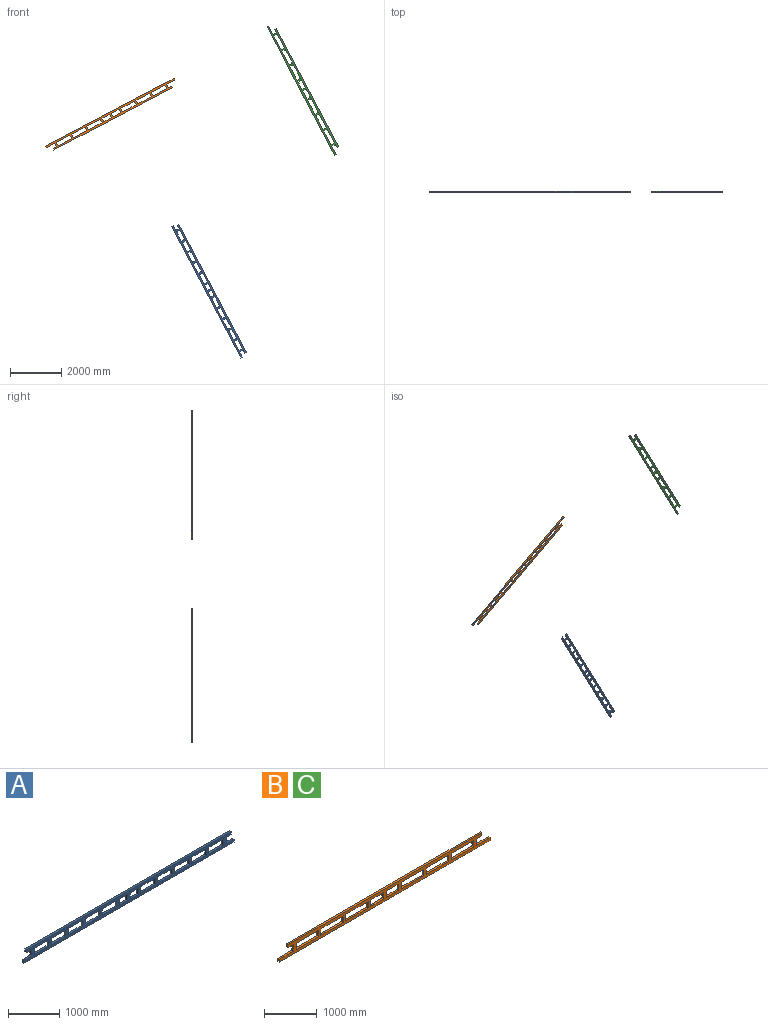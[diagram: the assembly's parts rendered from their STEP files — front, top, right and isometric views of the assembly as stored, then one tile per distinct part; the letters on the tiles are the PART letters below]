
ASSEMBLY  parts=3 mates=2
PART A: 62 faces, bbox 5800x45x290 mm
  f0: plane 400x45mm, normal (0,0,-1), area 18000mm2, adj f17,f18,f19,f23
  f1: plane 400x45mm, normal (0,0,-1), area 18000mm2, adj f17,f18,f22,f26
  f2: plane 400x45mm, normal (0,0,-1), area 18000mm2, adj f17,f18,f25,f29
  f3: plane 400x45mm, normal (0,0,-1), area 18000mm2, adj f17,f18,f28,f32
  f4: plane 400x45mm, normal (0,0,-1), area 18000mm2, adj f17,f18,f31,f35
  f5: plane 150x45mm, normal (0,0,-1), area 6750mm2, adj f14,f17,f18,f34
  f6: plane 225x45mm, normal (0,0,-1), area 10125mm2, adj f17,f18,f37,f59
  f7: plane 400x45mm, normal (0,0,-1), area 18000mm2, adj f17,f18,f38,f40
  f8: plane 400x45mm, normal (0,0,-1), area 18000mm2, adj f17,f18,f41,f52
  f9: plane 400x45mm, normal (0,0,-1), area 18000mm2, adj f17,f18,f53,f54
  f10: plane 400x45mm, normal (0,0,-1), area 18000mm2, adj f17,f18,f55,f56
  f11: plane 225x45mm, normal (0,0,-1), area 10125mm2, adj f17,f18,f20,f58
  f12: plane 400x45mm, normal (0,0,-1), area 18000mm2, adj f17,f18,f57,f60
  f13: plane 5660x45mm, normal (0,0,1), area 254700mm2, adj f14,f16,f17,f18
  f14: plane 70x45mm, normal (-1,0,0), area 3150mm2, adj f5,f13,f17,f18
  f15: plane 150x45mm, normal (0,0,-1), area 6750mm2, adj f16,f17,f18,f61
  f16: plane 70x45mm, normal (1,0,0), area 3150mm2, adj f13,f15,f17,f18
  f17: plane 5800x290mm, normal (0,-1,0), area 938700mm2, adj f0,f1,f2,f3,f4,f5,f6,f7
  f18: plane 5800x290mm, normal (0,1,0), area 938700mm2, adj f0,f1,f2,f3,f4,f5,f6,f7
  f19: plane 150x45mm, normal (-1,0,0), area 6750mm2, adj f0,f17,f18,f21
  f20: plane 150x45mm, normal (1,0,0), area 6750mm2, adj f11,f17,f18,f50
  f21: plane 400x45mm, normal (0,0,1), area 18000mm2, adj f17,f18,f19,f23
  f22: plane 150x45mm, normal (-1,0,0), area 6750mm2, adj f1,f17,f18,f24
  f23: plane 150x45mm, normal (1,0,0), area 6750mm2, adj f0,f17,f18,f21
  f24: plane 400x45mm, normal (0,0,1), area 18000mm2, adj f17,f18,f22,f26
  f25: plane 150x45mm, normal (-1,0,0), area 6750mm2, adj f2,f17,f18,f27
  f26: plane 150x45mm, normal (1,0,0), area 6750mm2, adj f1,f17,f18,f24
  f27: plane 400x45mm, normal (0,0,1), area 18000mm2, adj f17,f18,f25,f29
  f28: plane 150x45mm, normal (-1,0,0), area 6750mm2, adj f3,f17,f18,f30
  f29: plane 150x45mm, normal (1,0,0), area 6750mm2, adj f2,f17,f18,f27
  f30: plane 400x45mm, normal (0,0,1), area 18000mm2, adj f17,f18,f28,f32
  f31: plane 150x45mm, normal (-1,0,0), area 6750mm2, adj f4,f17,f18,f33
  f32: plane 150x45mm, normal (1,0,0), area 6750mm2, adj f3,f17,f18,f30
  f33: plane 400x45mm, normal (0,0,1), area 18000mm2, adj f17,f18,f31,f35
  f34: plane 150x45mm, normal (-1,0,0), area 6750mm2, adj f5,f17,f18,f36
  f35: plane 150x45mm, normal (1,0,0), area 6750mm2, adj f4,f17,f18,f33
  f36: plane 220x45mm, normal (0,0,1), area 9900mm2, adj f17,f18,f34,f51
  f37: plane 150x45mm, normal (-1,0,0), area 6750mm2, adj f6,f17,f18,f39
  f38: plane 150x45mm, normal (1,0,0), area 6750mm2, adj f7,f17,f18,f42
  f39: plane 225x45mm, normal (0,0,1), area 10125mm2, adj f17,f18,f37,f59
  f40: plane 150x45mm, normal (-1,0,0), area 6750mm2, adj f7,f17,f18,f42
  f41: plane 150x45mm, normal (1,0,0), area 6750mm2, adj f8,f17,f18,f44
  f42: plane 400x45mm, normal (0,0,1), area 18000mm2, adj f17,f18,f38,f40
  f43: plane 220x45mm, normal (0,0,1), area 9900mm2, adj f17,f18,f49,f61
  f44: plane 400x45mm, normal (0,0,1), area 18000mm2, adj f17,f18,f41,f52
  f45: plane 400x45mm, normal (0,0,1), area 18000mm2, adj f17,f18,f57,f60
  f46: plane 400x45mm, normal (0,0,1), area 18000mm2, adj f17,f18,f55,f56
  f47: plane 400x45mm, normal (0,0,1), area 18000mm2, adj f17,f18,f53,f54
  f48: plane 5800x45mm, normal (0,0,-1), area 261000mm2, adj f17,f18,f49,f51
  f49: plane 70x45mm, normal (1,0,0), area 3150mm2, adj f17,f18,f43,f48
  f50: plane 225x45mm, normal (0,0,1), area 10125mm2, adj f17,f18,f20,f58
  f51: plane 70x45mm, normal (-1,0,0), area 3150mm2, adj f17,f18,f36,f48
  f52: plane 150x45mm, normal (-1,0,0), area 6750mm2, adj f8,f17,f18,f44
  f53: plane 150x45mm, normal (1,0,0), area 6750mm2, adj f9,f17,f18,f47
  f54: plane 150x45mm, normal (-1,0,0), area 6750mm2, adj f9,f17,f18,f47
  f55: plane 150x45mm, normal (1,0,0), area 6750mm2, adj f10,f17,f18,f46
  f56: plane 150x45mm, normal (-1,0,0), area 6750mm2, adj f10,f17,f18,f46
  f57: plane 150x45mm, normal (1,0,0), area 6750mm2, adj f12,f17,f18,f45
  f58: plane 150x45mm, normal (-1,0,0), area 6750mm2, adj f11,f17,f18,f50
  f59: plane 150x45mm, normal (1,0,0), area 6750mm2, adj f6,f17,f18,f39
  f60: plane 150x45mm, normal (-1,0,0), area 6750mm2, adj f12,f17,f18,f45
  f61: plane 150x45mm, normal (1,0,0), area 6750mm2, adj f15,f17,f18,f43
PART B: 46 faces, bbox 5660x45x290 mm
  f0: plane 600x45mm, normal (0,0,1), area 27000mm2, adj f13,f14,f29,f44
  f1: plane 600x45mm, normal (0,0,1), area 27000mm2, adj f13,f14,f31,f32
  f2: plane 600x45mm, normal (0,0,1), area 27000mm2, adj f13,f14,f33,f34
  f3: plane 600x45mm, normal (0,0,1), area 27000mm2, adj f13,f14,f35,f36
  f4: plane 345x45mm, normal (0,0,1), area 15525mm2, adj f13,f14,f37,f38
  f5: plane 345x45mm, normal (0,0,1), area 15525mm2, adj f13,f14,f28,f39
  f6: plane 370x45mm, normal (0,0,1), area 16650mm2, adj f10,f13,f14,f41
  f7: plane 600x45mm, normal (0,0,1), area 27000mm2, adj f13,f14,f40,f43
  f8: plane 600x45mm, normal (0,0,1), area 27000mm2, adj f13,f14,f42,f45
  f9: plane 5660x45mm, normal (0,0,-1), area 254700mm2, adj f10,f12,f13,f14
  f10: plane 70x45mm, normal (1,0,0), area 3150mm2, adj f6,f9,f13,f14
  f11: plane 370x45mm, normal (0,0,1), area 16650mm2, adj f12,f13,f14,f30
  f12: plane 70x45mm, normal (-1,0,0), area 3150mm2, adj f9,f11,f13,f14
  f13: plane 5660x290mm, normal (0,-1,0), area 856100mm2, adj f0,f1,f2,f3,f4,f5,f6,f7
  f14: plane 5660x290mm, normal (0,1,0), area 856100mm2, adj f0,f1,f2,f3,f4,f5,f6,f7
  f15: plane 600x45mm, normal (0,0,-1), area 27000mm2, adj f13,f14,f29,f44
  f16: plane 600x45mm, normal (0,0,-1), area 27000mm2, adj f13,f14,f42,f45
  f17: plane 600x45mm, normal (0,0,-1), area 27000mm2, adj f13,f14,f40,f43
  f18: plane 345x45mm, normal (0,0,-1), area 15525mm2, adj f13,f14,f37,f38
  f19: plane 600x45mm, normal (0,0,-1), area 27000mm2, adj f13,f14,f35,f36
  f20: plane 600x45mm, normal (0,0,-1), area 27000mm2, adj f13,f14,f33,f34
  f21: plane 600x45mm, normal (0,0,-1), area 27000mm2, adj f13,f14,f31,f32
  f22: plane 150x45mm, normal (0,0,-1), area 6750mm2, adj f13,f14,f25,f30
  f23: plane 345x45mm, normal (0,0,-1), area 15525mm2, adj f13,f14,f28,f39
  f24: plane 5220x45mm, normal (0,0,1), area 234900mm2, adj f13,f14,f25,f27
  f25: plane 70x45mm, normal (-1,0,0), area 3150mm2, adj f13,f14,f22,f24
  f26: plane 150x45mm, normal (0,0,-1), area 6750mm2, adj f13,f14,f27,f41
  f27: plane 70x45mm, normal (1,0,0), area 3150mm2, adj f13,f14,f24,f26
  f28: plane 150x45mm, normal (-1,0,0), area 6750mm2, adj f5,f13,f14,f23
  f29: plane 150x45mm, normal (1,0,0), area 6750mm2, adj f0,f13,f14,f15
  f30: plane 150x45mm, normal (-1,0,0), area 6750mm2, adj f11,f13,f14,f22
  f31: plane 150x45mm, normal (1,0,0), area 6750mm2, adj f1,f13,f14,f21
  f32: plane 150x45mm, normal (-1,0,0), area 6750mm2, adj f1,f13,f14,f21
  f33: plane 150x45mm, normal (1,0,0), area 6750mm2, adj f2,f13,f14,f20
  f34: plane 150x45mm, normal (-1,0,0), area 6750mm2, adj f2,f13,f14,f20
  f35: plane 150x45mm, normal (1,0,0), area 6750mm2, adj f3,f13,f14,f19
  f36: plane 150x45mm, normal (-1,0,0), area 6750mm2, adj f3,f13,f14,f19
  f37: plane 150x45mm, normal (1,0,0), area 6750mm2, adj f4,f13,f14,f18
  f38: plane 150x45mm, normal (-1,0,0), area 6750mm2, adj f4,f13,f14,f18
  f39: plane 150x45mm, normal (1,0,0), area 6750mm2, adj f5,f13,f14,f23
  f40: plane 150x45mm, normal (-1,0,0), area 6750mm2, adj f7,f13,f14,f17
  f41: plane 150x45mm, normal (1,0,0), area 6750mm2, adj f6,f13,f14,f26
  f42: plane 150x45mm, normal (-1,0,0), area 6750mm2, adj f8,f13,f14,f16
  f43: plane 150x45mm, normal (1,0,0), area 6750mm2, adj f7,f13,f14,f17
  f44: plane 150x45mm, normal (-1,0,0), area 6750mm2, adj f0,f13,f14,f15
  f45: plane 150x45mm, normal (1,0,0), area 6750mm2, adj f8,f13,f14,f16
PART C: same geometry as B
PLACE A rot(axis=(0,1,0),62.3deg) t=(-2376.62,-655.01,-2951.59)mm
PLACE B rot(axis=(0,1,0),152.3deg) t=(-6147.49,-655.01,4006.62)mm
PLACE C rot(axis=(0,1,0),62.3deg) t=(1311.33,-662.51,4876.02)mm
MATE parallel C.f27 <-> B.f11  axis (0.47,0,-0.89) through (2720.9,-662.51,2668.4)mm
MATE parallel B.f12 <-> A.f36  axis (0.89,0,0.47) through (-3642.75,-655.01,5323.88)mm
